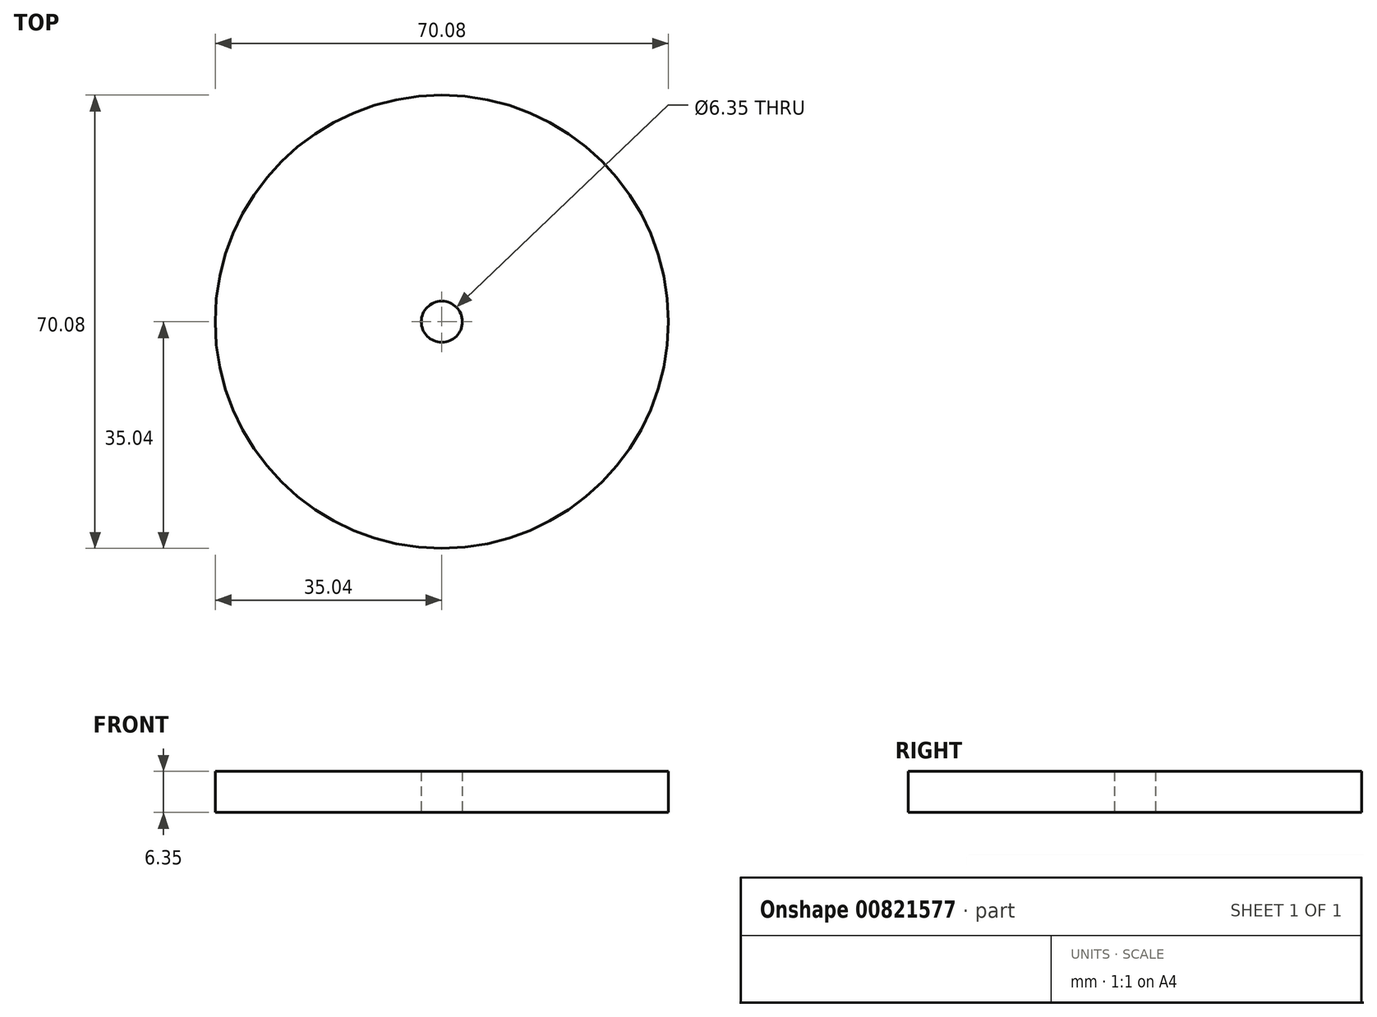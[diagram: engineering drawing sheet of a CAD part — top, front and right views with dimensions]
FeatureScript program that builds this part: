
annotation { "Feature Type Name" : "Feature", "Feature Type Description" : "" }
export const myFeature = defineFeature(function(context is Context, id is Id, definition is map)
    precondition{}
    {
        {
            var Q0;
            Q0=qCreatedBy(makeId("Top.planeOp"),FACE);
            var sketch = newSketch(context, id + "F0", { "sketchPlane" : qUnion([Q0])});
            skCircle(sketch, "E0", {"center": v(0, 0) * mm, "radius": 35.04 * mm});
            skCircle(sketch, "E1", {"center": v(0, 0) * mm, "radius": 3.18 * mm});
            skSolve(sketch);
        }
        {
            var Q0;
            Q0 = qSketchRegion(id + "F0", true);
            extrude(context, id + "F1", {"entities" : qUnion([Q0]), "depth" : 6.35 * mm, "offsetDistance" : 25.4 * mm});
        }
    });
